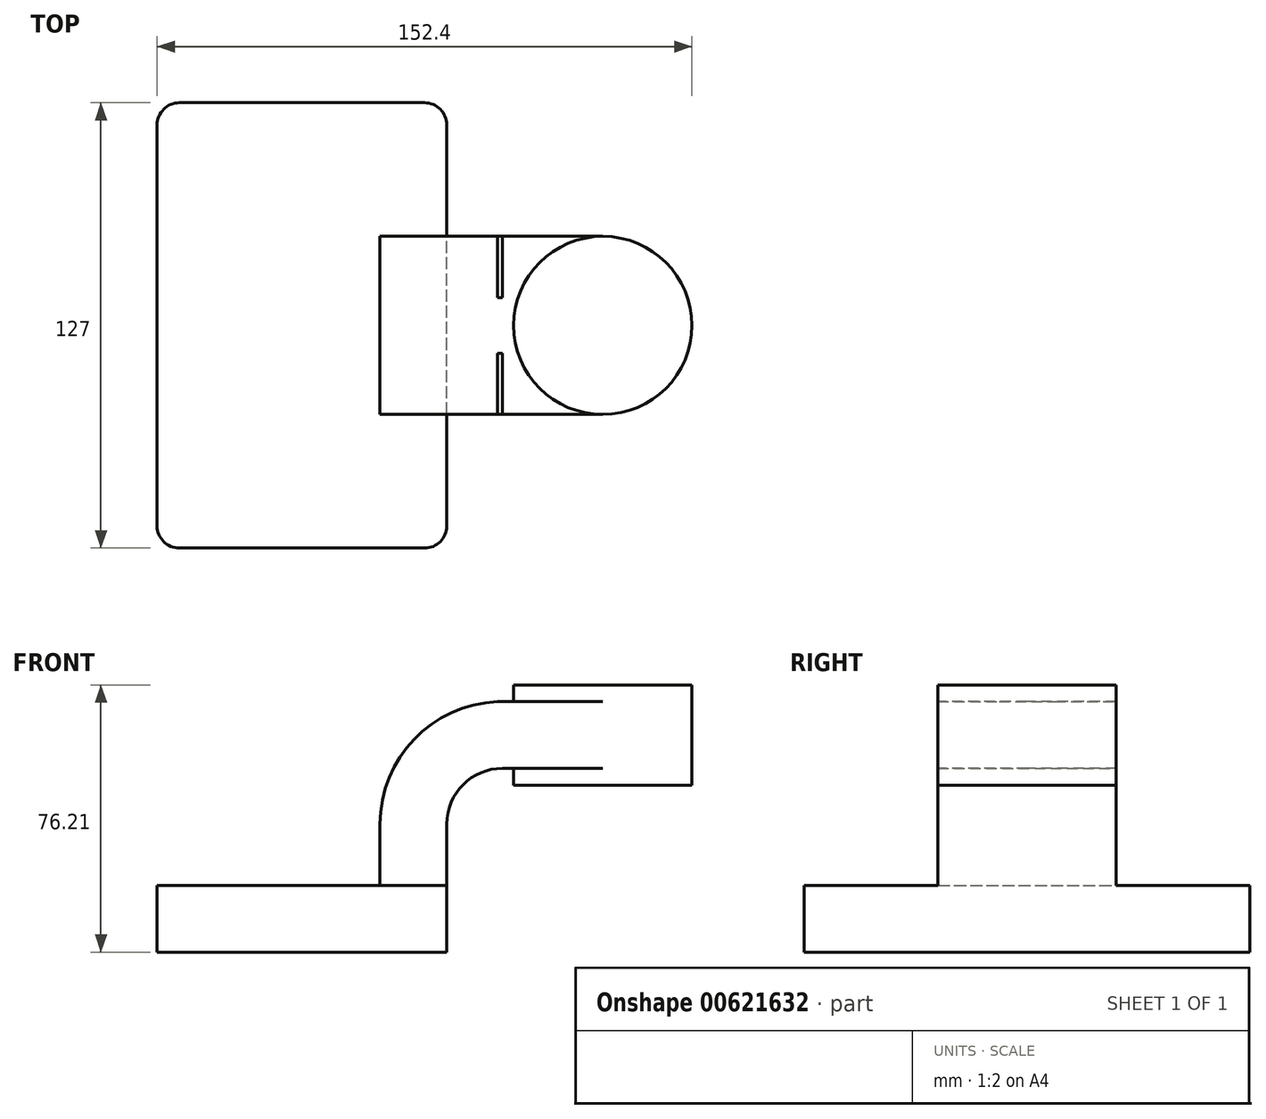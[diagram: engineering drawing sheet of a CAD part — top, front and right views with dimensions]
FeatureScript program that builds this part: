
annotation { "Feature Type Name" : "Feature", "Feature Type Description" : "" }
export const myFeature = defineFeature(function(context is Context, id is Id, definition is map)
    precondition{}
    {
        {
            var Q0;
            Q0=qCreatedBy(makeId("Front.planeOp"),FACE);
            var sketch = newSketch(context, id + "F0", { "sketchPlane" : qUnion([Q0])});
            skLineSegment(sketch, "E0.bottom", {"start": v(-41.28, -9.53) * mm, "end": v(41.28, -9.53) * mm});
            skLineSegment(sketch, "E0.top", {"start": v(-41.28, 9.52) * mm, "end": v(41.28, 9.52) * mm});
            skLineSegment(sketch, "E0.left", {"start": v(-41.28, -9.53) * mm, "end": v(-41.28, 9.53) * mm});
            skLineSegment(sketch, "E0.right", {"start": v(41.28, -9.53) * mm, "end": v(41.28, 9.52) * mm});
            skPoint(sketch, "E0.middle", {"position": v(0, 0) * mm});
            skLineSegment(sketch, "E1.bottom", {"start": v(60.32, 38.1) * mm, "end": v(111.12, 38.1) * mm});
            skLineSegment(sketch, "E1.top", {"start": v(60.32, 66.67) * mm, "end": v(111.12, 66.67) * mm});
            skLineSegment(sketch, "E1.left", {"start": v(60.32, 38.1) * mm, "end": v(60.32, 66.67) * mm});
            skLineSegment(sketch, "E1.right", {"start": v(111.12, 38.1) * mm, "end": v(111.12, 66.67) * mm});
            skPoint(sketch, "E1.middle", {"position": v(85.72, 52.39) * mm});
            skLineSegment(sketch, "E2", {"start": v(41.28, 9.52) * mm, "end": v(41.28, 27) * mm});
            skArc(sketch, "E3", {"start": v(41.27, 27) * mm, "mid": v(45.92, 38.23) * mm, "end": v(57.15, 42.88) * mm});
            skLineSegment(sketch, "E4", {"start": v(57.15, 42.88) * mm, "end": v(86.04, 42.88) * mm});
            skLineSegment(sketch, "E5.0", {"start": v(57.15, 61.93) * mm, "end": v(86.04, 61.93) * mm});
            skArc(sketch, "E5.1", {"start": v(22.23, 27) * mm, "mid": v(32.45, 51.7) * mm, "end": v(57.15, 61.93) * mm});
            skLineSegment(sketch, "E5.2", {"start": v(22.22, 9.52) * mm, "end": v(22.22, 27) * mm});
            skFitSpline(sketch, "E6", {"points": [v(-41.28, 9.53) * mm, v(57.15, 61.93) * mm], "startDerivative": vector(2.35, 127.43) * mm, "endDerivative": vector(106.73, 1.87) * mm});
            skLineSegment(sketch, "E7", {"start": v(85.72, 38.1) * mm, "end": v(85.72, 66.67) * mm});
            skSolve(sketch);
        }
        {
            var Q0;
            Q0=makeQuery(id+"F0.imprint","IMPRINT",FACE,{"disambiguationData":[TD([[makeQuery(id+"F0.imprint","IMPRINT",EDGE,{"derivedFrom":sQuery(id+"F0.wireOp",EDGE,"E0.bottom")}),1.0]])]});
            extrude(context, id + "F1", {"entities" : qUnion([Q0]), "endBound" : BoundingType.SYMMETRIC, "depth" : 127 * mm, "offsetDistance" : 25.4 * mm});
        }
        {
            var Q0;
            {var subQ1=sQuery(id+"F0.wireOp",EDGE,"E2");Q0=makeQuery(id+"F0.imprint","IMPRINT",FACE,{"disambiguationData":[TD([[makeQuery(id+"F0.imprint","IMPRINT",EDGE,{"derivedFrom":subQ1}),1.0]])]});}
            var Q1;
            {var subQ0=sQuery(id+"F0.wireOp",EDGE,"E4");var subQ1=sQuery(id+"F0.wireOp",EDGE,"E1.left");var subQ2=makeQuery(id+"F0.imprint","INTERSECT",VERTEX,{"derivedFrom":[subQ1,subQ0]});Q1=makeQuery(id+"F0.imprint","IMPRINT",FACE,{"disambiguationData":[TD([[makeQuery(id+"F0.imprint","IMPRINT",EDGE,{"disambiguationData":[TD([[subQ2,-1.0]])],"derivedFrom":subQ1}),-1.0]])]});}
            extrude(context, id + "F2", {"entities" : qUnion([Q0, Q1]), "operationType" : NewBodyOperationType.ADD, "endBound" : BoundingType.SYMMETRIC, "depth" : 50.8 * mm, "offsetDistance" : 25.4 * mm});
        }
        {
            var Q0;
            Q0=makeQuery(id+"F0.imprint","IMPRINT",FACE,{"disambiguationData":[TD([[makeQuery(id+"F0.imprint","IMPRINT",EDGE,{"derivedFrom":sQuery(id+"F0.wireOp",EDGE,"E5.1")}),1.0]])]});
            extrude(context, id + "F3", {"entities" : qUnion([Q0]), "operationType" : NewBodyOperationType.ADD, "endBound" : BoundingType.SYMMETRIC, "depth" : 15.88 * mm, "offsetDistance" : 25.4 * mm});
        }
        {
            var Q0;
            {var subQ4=sQuery(id+"F0.wireOp",EDGE,"E1.right");Q0=makeQuery(id+"F0.imprint","IMPRINT",FACE,{"disambiguationData":[TD([[makeQuery(id+"F0.imprint","IMPRINT",EDGE,{"derivedFrom":subQ4}),1.0]])]});}
            var Q1;
            Q1=sQuery(id+"F0.wireOp",EDGE,"E7");
            revolve(context, id + "F4", {"operationType" : NewBodyOperationType.ADD, "entities" : qUnion([Q0]), "axis" : qUnion([Q1]), "revolveType" : RevolveType.FULL});
        }
        {
            var Q0;
            Q0=makeQuery(id+"F1.opExtrude","CAP_EDGE",EDGE,{"disambiguationData":[OSD([sQuery(id+"F0.wireOp",EDGE,"E0.right")])],"isStart":false});
            var Q1;
            Q1=makeQuery(id+"F1.opExtrude","CAP_EDGE",EDGE,{"disambiguationData":[OSD([sQuery(id+"F0.wireOp",EDGE,"E0.left")])],"isStart":false});
            var Q2;
            Q2=makeQuery(id+"F1.opExtrude","CAP_EDGE",EDGE,{"disambiguationData":[OSD([sQuery(id+"F0.wireOp",EDGE,"E0.left")])],"isStart":true});
            var Q3;
            Q3=makeQuery(id+"F1.opExtrude","CAP_EDGE",EDGE,{"disambiguationData":[OSD([sQuery(id+"F0.wireOp",EDGE,"E0.right")])],"isStart":true});
            fillet(context, id + "F5", {"entities" : qUnion([Q0, Q1, Q2, Q3]), "radius" : 6.35 * mm, "tangentPropagation" : true, "allowEdgeOverflow" : false});
        }
    });
